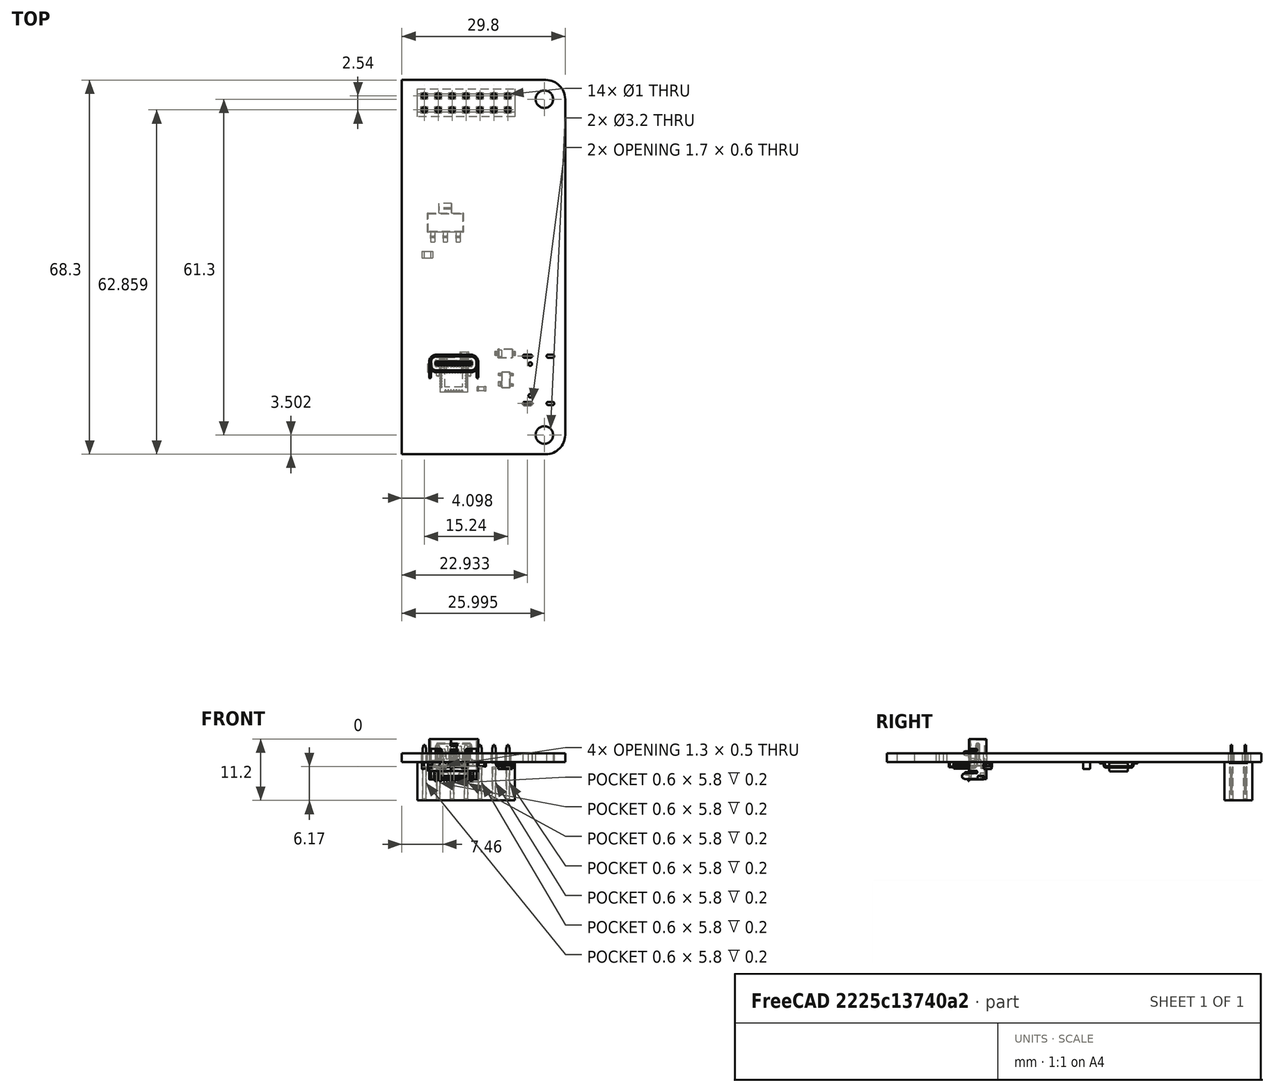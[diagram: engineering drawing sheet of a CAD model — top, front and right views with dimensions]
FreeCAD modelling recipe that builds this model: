
FCSTD DOCUMENT  (FreeCAD 1.0R39109 (Git))
Label: hautDeForme
License: All rights reserved
LicenseURL: http://en.wikipedia.org/wiki/All_rights_reserved
objects: Part::Feature×54, App::Link×18, App::Part×6, PartDesign::CoordinateSystem×1, Sketcher::SketchObject×1
note: 57 computed .brp shape members not serialized (recipe doc carries the construction recipe); baked Part::Feature solids carry a one-line shape summary decoded from their .brp

FEATURE [PartDesign::CoordinateSystem] Local_CS_adfa
  AttacherType = Attacher::AttachEngine3D
  MapMode = 2
FEATURE [Part::Feature] Pcb_adfa
  Placement = pos=(-130.277,147.371,0) rot=(0,0,1;0rad)
  shape: bbox 29.8 x 68.3 x 1.6 mm, 50 faces (baked)
FEATURE [Sketcher::SketchObject] PCB_Sketch_adfa
  ArcFitTolerance = 1e-06
  FullyConstrained = false
  MakeInternals = false
  sketch-geometry (6):
    g0: LineSegment StartX=-9.4646 StartY=-14.8382 StartZ=0 EndX=-9.4646 EndY=53.4618 EndZ=0
    g1: LineSegment StartX=16.8354 StartY=53.4618 StartZ=0 EndX=-9.4646 EndY=53.4618 EndZ=0
    g2: LineSegment StartX=20.3354 StartY=49.9618 StartZ=0 EndX=20.3354 EndY=-11.3382 EndZ=0
    g3: LineSegment StartX=16.8354 StartY=-14.8382 StartZ=0 EndX=-9.4646 EndY=-14.8382 EndZ=0
    g4: ArcOfCircle CenterX=16.8354 CenterY=49.9618 CenterZ=0 NormalX=0 NormalY=0 NormalZ=-1 AngleXU=1.5708 Radius=3.5 StartAngle=0 EndAngle=1.5708
    g5: ArcOfCircle CenterX=16.8354 CenterY=-11.3382 CenterZ=0 NormalX=0 NormalY=0 NormalZ=-1 AngleXU=3.14159 Radius=3.5 StartAngle=0 EndAngle=1.5708
  constraints (6):
    c: Coincident(g0,g3)
    c: Coincident(g0,g1)
    c: Coincident(g3,g5)
    c: Coincident(g1,g4)
    c: Coincident(g2,g5)
    c: Coincident(g2,g4)
FEATURE [App::Part] Board_Geoms_adfa
  Group = -> [Pcb_adfa,PCB_Sketch_adfa]
  Origin = -> Origin
FEATURE [Part::Feature] Shape  label="C14_C_0603_1608Metric_466b06563dad"
  Placement = pos=(5.08,-2.921,-1.6) rot=(0,1,0;3.14159rad)
  shape: bbox 1.6 x 0.8 x 0.8 mm, 28 faces (baked)
FEATURE [Part::Feature] Shape001  label="C6_C_0805_2012Metric_36fd2068b96d"
  Placement = pos=(-4.826,21.59,-1.6) rot=(1,0,0;3.14159rad)
  shape: bbox 2 x 1.25 x 1.25 mm, 28 faces (baked)
FEATURE [Part::Feature] Shape002  label="R26_R_0603_1608Metric_7708bdc434fe"
  Placement = pos=(1.905,3.429,-1.6) rot=(1,0,0;3.14159rad)
  shape: bbox 1.6 x 0.8 x 0.45 mm, 26 faces (baked)
FEATURE [App::Link] C6_C_0805_2012Metric_36fd2068b96d_ln_  label="C16_C_0805_2012Metric_426e6888749c"
  LinkPlacement = pos=(9.652,5.969,-1.6) rot=(1,0,0;3.14159rad)
  LinkedObject = -> Shape001
  Placement = pos=(9.652,5.969,-1.6) rot=(1,0,0;3.14159rad)
FEATURE [App::Link] C6_C_0805_2012Metric_36fd2068b96d_ln_001  label="C7_C_0805_2012Metric_e14df2acbac5"
  LinkPlacement = pos=(-0.635,21.59,-1.6) rot=(0,1,0;3.14159rad)
  LinkedObject = -> Shape001
  Placement = pos=(-0.635,21.59,-1.6) rot=(0,1,0;3.14159rad)
FEATURE [App::Link] R26_R_0603_1608Metric_7708bdc434fe_ln_  label="R24_R_0603_1608Metric_e1f34a9d9af8"
  LinkPlacement = pos=(0.508,-6.096,-1.6) rot=(0.707107,-0.707107,0;3.14159rad)
  LinkedObject = -> Shape002
  Placement = pos=(0.508,-6.096,-1.6) rot=(0.707107,-0.707107,0;3.14159rad)
FEATURE [Part::Feature] Shape003  label="D9_LED_0603_1608Metric_46d654ef8e3e"
  Placement = pos=(-4.318,0.889,-1.6) rot=(0.707107,0.707107,0;3.14159rad)
  shape: bbox 0.8 x 1.6 x 1.1 mm, 50 faces (baked)
FEATURE [Part::Feature] Shape004  label="J1_PinSocket_2x07_P254mm_Vertical_6ab3e544b67c"
  Placement = pos=(9.8784,50.5588,-1.6) rot=(0.707107,0.707107,0;3.14159rad)
  shape: bbox 17.78 x 5.08 x 10.1 mm, 444 faces (baked)
FEATURE [App::Link] C14_C_0603_1608Metric_466b06563dad_ln_  label="C15_C_0603_1608Metric_0d21c20a43dc"
  LinkPlacement = pos=(5.969,4.318,-1.6) rot=(0.707107,-0.707107,0;3.14159rad)
  LinkedObject = -> Shape
  Placement = pos=(5.969,4.318,-1.6) rot=(0.707107,-0.707107,0;3.14159rad)
FEATURE [Part::Feature] Shape005  label="U2_SOT_223_cc65569aa0fe"
  Placement = pos=(-1.524,27.432,-1.6) rot=(0.707107,0.707107,0;3.14159rad)
  shape: bbox 6.5 x 7 x 1.7 mm, 78 faces (baked)
FEATURE [App::Link] R26_R_0603_1608Metric_7708bdc434fe_ln_001  label="R27_R_0603_1608Metric_c96fc7131dde"
  LinkPlacement = pos=(-1.397,3.429,-1.6) rot=(0,1,0;3.14159rad)
  LinkedObject = -> Shape002
  Placement = pos=(-1.397,3.429,-1.6) rot=(0,1,0;3.14159rad)
FEATURE [App::Link] R26_R_0603_1608Metric_7708bdc434fe_ln_002  label="R35_R_0603_1608Metric_f47ad657d3cf"
  LinkPlacement = pos=(-6.096,-2.413,-1.6) rot=(0.707107,-0.707107,0;3.14159rad)
  LinkedObject = -> Shape002
  Placement = pos=(-6.096,-2.413,-1.6) rot=(0.707107,-0.707107,0;3.14159rad)
FEATURE [App::Link] R26_R_0603_1608Metric_7708bdc434fe_ln_003  label="R34_R_0603_1608Metric_230fafb0b39b"
  LinkPlacement = pos=(-6.096,0.889,-1.6) rot=(0.707107,0.707107,0;3.14159rad)
  LinkedObject = -> Shape002
  Placement = pos=(-6.096,0.889,-1.6) rot=(0.707107,0.707107,0;3.14159rad)
FEATURE [App::Link] R26_R_0603_1608Metric_7708bdc434fe_ln_004  label="R29_R_0603_1608Metric_0ce4d2b71c9b"
  LinkPlacement = pos=(12.573,-7.366,-1.6) rot=(0,1,0;3.14159rad)
  LinkedObject = -> Shape002
  Placement = pos=(12.573,-7.366,-1.6) rot=(0,1,0;3.14159rad)
FEATURE [App::Link] R26_R_0603_1608Metric_7708bdc434fe_ln_005  label="R25_R_0603_1608Metric_e44b7830c810"
  LinkPlacement = pos=(-1.27,-6.096,-1.6) rot=(0.707107,0.707107,0;3.14159rad)
  LinkedObject = -> Shape002
  Placement = pos=(-1.27,-6.096,-1.6) rot=(0.707107,0.707107,0;3.14159rad)
FEATURE [Part::Feature] Shape006  label="U4_QFN-28-1EP_5x5mm_Pitch0.5mm_e0a1b5ef8927"
  Placement = pos=(2e-16,-1.016,-1.6) rot=(0,1,0;3.14159rad)
  shape: bbox 5 x 5 x 0.92 mm, 182 faces (baked)
FEATURE [Part::Feature] Shape007  label="D14_D_SOD_123_b6459e2e886b"
  Placement = pos=(9.398,3.556,-1.6) rot=(1,0,0;3.14159rad)
  shape: bbox 3.8 x 1.6 x 1.25 mm, 67 faces (baked)
FEATURE [Part::Feature] Part__Feature  label="USB4105GFA_USB4105GFA"
  Placement = pos=(0,3e-16,-1.255) rot=(0,0,1;0rad)
  shape: bbox 0.25 x 0.05 x 2.38 mm, 6 faces (baked)
FEATURE [Part::Feature] Part__Feature001  label="USB4105GFA_USB4105GFA001"
  Placement = pos=(0,3e-16,-1.255) rot=(0,0,1;0rad)
  shape: bbox 0.25 x 0.05 x 2.38 mm, 6 faces (baked)
FEATURE [Part::Feature] Part__Feature002  label="USB4105GFA_USB4105GFA002"
  Placement = pos=(0,3e-16,-1.255) rot=(0,0,1;0rad)
  shape: bbox 0.25 x 0.05 x 1.88 mm, 6 faces (baked)
FEATURE [Part::Feature] Part__Feature003  label="USB4105GFA_USB4105GFA003"
  Placement = pos=(0,3e-16,-1.255) rot=(0,0,1;0rad)
  shape: bbox 0.25 x 0.05 x 1.88 mm, 6 faces (baked)
FEATURE [Part::Feature] Part__Feature004  label="USB4105GFA_USB4105GFA004"
  Placement = pos=(0,3e-16,-1.255) rot=(0,0,1;0rad)
  shape: bbox 0.25 x 0.05 x 1.88 mm, 6 faces (baked)
FEATURE [Part::Feature] Part__Feature005  label="USB4105GFA_USB4105GFA005"
  Placement = pos=(0,3e-16,-1.255) rot=(0,0,1;0rad)
  shape: bbox 0.25 x 0.05 x 1.88 mm, 6 faces (baked)
FEATURE [Part::Feature] Part__Feature006  label="USB4105GFA_USB4105GFA006"
  Placement = pos=(0,3e-16,-1.255) rot=(0,0,1;0rad)
  shape: bbox 0.25 x 0.05 x 1.88 mm, 6 faces (baked)
FEATURE [Part::Feature] Part__Feature007  label="USB4105GFA_USB4105GFA007"
  Placement = pos=(0,3e-16,-1.255) rot=(0,0,1;0rad)
  shape: bbox 0.25 x 0.05 x 1.88 mm, 6 faces (baked)
FEATURE [Part::Feature] Part__Feature008  label="USB4105GFA_USB4105GFA008"
  Placement = pos=(0,3e-16,-1.255) rot=(0,0,1;0rad)
  shape: bbox 0.25 x 0.05 x 1.88 mm, 6 faces (baked)
FEATURE [Part::Feature] Part__Feature009  label="USB4105GFA_USB4105GFA009"
  Placement = pos=(0,3e-16,-1.255) rot=(0,0,1;0rad)
  shape: bbox 0.25 x 0.05 x 1.88 mm, 6 faces (baked)
FEATURE [Part::Feature] Part__Feature010  label="USB4105GFA_USB4105GFA010"
  Placement = pos=(0,3e-16,-1.255) rot=(0,0,1;0rad)
  shape: bbox 0.25 x 0.05 x 2.38 mm, 6 faces (baked)
FEATURE [Part::Feature] Part__Feature011  label="USB4105GFA_USB4105GFA011"
  Placement = pos=(0,3e-16,-1.255) rot=(0,0,1;0rad)
  shape: bbox 0.25 x 0.05 x 2.38 mm, 6 faces (baked)
FEATURE [Part::Feature] Part__Feature012  label="USB4105GFA_USB4105GFA012"
  Placement = pos=(0,3e-16,-1.255) rot=(0,0,1;0rad)
  shape: bbox 0.25 x 0.05 x 2.38 mm, 6 faces (baked)
FEATURE [Part::Feature] Part__Feature013  label="USB4105GFA_USB4105GFA013"
  Placement = pos=(0,3e-16,-1.255) rot=(0,0,1;0rad)
  shape: bbox 0.25 x 0.05 x 1.88 mm, 6 faces (baked)
FEATURE [Part::Feature] Part__Feature014  label="USB4105GFA_USB4105GFA014"
  Placement = pos=(0,3e-16,-1.255) rot=(0,0,1;0rad)
  shape: bbox 0.25 x 0.05 x 1.88 mm, 6 faces (baked)
FEATURE [Part::Feature] Part__Feature015  label="USB4105GFA_USB4105GFA015"
  Placement = pos=(0,3e-16,-1.255) rot=(0,0,1;0rad)
  shape: bbox 0.25 x 0.05 x 2.38 mm, 6 faces (baked)
FEATURE [Part::Feature] Part__Feature016  label="USB4105GFA_USB4105GFA016"
  Placement = pos=(0,3e-16,-1.255) rot=(0,0,1;0rad)
  shape: bbox 0.25 x 0.05 x 1.88 mm, 6 faces (baked)
FEATURE [Part::Feature] Part__Feature017  label="USB4105GFA_USB4105GFA017"
  Placement = pos=(0,3e-16,-1.255) rot=(0,0,1;0rad)
  shape: bbox 0.25 x 0.05 x 1.88 mm, 6 faces (baked)
FEATURE [Part::Feature] Part__Feature018  label="USB4105GFA_USB4105GFA018"
  Placement = pos=(0,3e-16,-1.255) rot=(0,0,1;0rad)
  shape: bbox 0.25 x 0.05 x 1.88 mm, 6 faces (baked)
FEATURE [Part::Feature] Part__Feature019  label="USB4105GFA_USB4105GFA019"
  Placement = pos=(0,3e-16,-1.255) rot=(0,0,1;0rad)
  shape: bbox 0.25 x 0.05 x 1.88 mm, 6 faces (baked)
FEATURE [Part::Feature] Part__Feature020  label="USB4105GFA_USB4105GFA020"
  Placement = pos=(0,3e-16,-1.255) rot=(0,0,1;0rad)
  shape: bbox 0.25 x 0.05 x 2.38 mm, 6 faces (baked)
FEATURE [Part::Feature] Part__Feature021  label="USB4105GFA_USB4105GFA021"
  Placement = pos=(0,3e-16,-1.255) rot=(0,0,1;0rad)
  shape: bbox 0.25 x 0.05 x 1.88 mm, 6 faces (baked)
FEATURE [Part::Feature] Part__Feature022  label="USB4105GFA_USB4105GFA022"
  Placement = pos=(0,3e-16,-1.255) rot=(0,0,1;0rad)
  shape: bbox 0.25 x 0.05 x 1.88 mm, 6 faces (baked)
FEATURE [Part::Feature] Part__Feature023  label="USB4105GFA_USB4105GFA023"
  Placement = pos=(0,3e-16,-1.255) rot=(0,0,1;0rad)
  shape: bbox 0.25 x 0.05 x 2.38 mm, 6 faces (baked)
FEATURE [Part::Feature] Part__Feature024  label="USB4105GFA_USB4105GFA024"
  Placement = pos=(0,3e-16,-1.255) rot=(0,0,1;0rad)
  shape: bbox 0.35 x 0.1 x 1.82 mm, 9 faces (baked)
FEATURE [Part::Feature] Part__Feature025  label="USB4105GFA_USB4105GFA025"
  Placement = pos=(0,3e-16,-1.255) rot=(0,0,1;0rad)
  shape: bbox 0.35 x 0.1 x 1.82 mm, 9 faces (baked)
FEATURE [Part::Feature] Part__Feature026  label="USB4105GFA_USB4105GFA026"
  Placement = pos=(0,3e-16,-1.255) rot=(0,0,1;0rad)
  shape: bbox 0.2 x 0.32 x 0.725 mm, 10 faces (baked)
FEATURE [Part::Feature] Part__Feature027  label="USB4105GFA_USB4105GFA027"
  Placement = pos=(0,3e-16,-1.255) rot=(0,0,1;0rad)
  shape: bbox 0.2 x 0.32 x 0.725 mm, 10 faces (baked)
FEATURE [Part::Feature] Part__Feature028  label="USB4105GFA_USB4105GFA028"
  Placement = pos=(0,3e-16,-1.255) rot=(0,0,1;0rad)
  shape: bbox 0.2 x 0.32 x 0.725 mm, 10 faces (baked)
FEATURE [Part::Feature] Part__Feature029  label="USB4105GFA_USB4105GFA029"
  Placement = pos=(0,3e-16,-1.255) rot=(0,0,1;0rad)
  shape: bbox 0.2 x 0.32 x 0.725 mm, 10 faces (baked)
FEATURE [Part::Feature] Part__Feature030  label="USB4105GFA_USB4105GFA030"
  Placement = pos=(0,3e-16,-1.255) rot=(0,0,1;0rad)
  shape: bbox 0.2 x 0.32 x 0.725 mm, 10 faces (baked)
FEATURE [Part::Feature] Part__Feature031  label="USB4105GFA_USB4105GFA031"
  Placement = pos=(0,3e-16,-1.255) rot=(0,0,1;0rad)
  shape: bbox 0.2 x 0.32 x 0.725 mm, 10 faces (baked)
FEATURE [Part::Feature] Part__Feature032  label="USB4105GFA_USB4105GFA032"
  Placement = pos=(0,3e-16,-1.255) rot=(0,0,1;0rad)
  shape: bbox 0.2 x 0.32 x 0.725 mm, 10 faces (baked)
FEATURE [Part::Feature] Part__Feature033  label="USB4105GFA_USB4105GFA033"
  Placement = pos=(0,3e-16,-1.255) rot=(0,0,1;0rad)
  shape: bbox 0.2 x 0.32 x 0.725 mm, 10 faces (baked)
FEATURE [Part::Feature] Part__Feature034  label="USB4105GFA_USB4105GFA034"
  Placement = pos=(0,3e-16,-1.255) rot=(0,0,1;0rad)
  shape: bbox 0.2 x 0.32 x 0.725 mm, 10 faces (baked)
FEATURE [Part::Feature] Part__Feature035  label="USB4105GFA_USB4105GFA035"
  Placement = pos=(0,3e-16,-1.255) rot=(0,0,1;0rad)
  shape: bbox 0.2 x 0.32 x 0.725 mm, 10 faces (baked)
FEATURE [Part::Feature] Part__Feature036  label="USB4105GFA_USB4105GFA036"
  Placement = pos=(0,3e-16,-1.255) rot=(0,0,1;0rad)
  shape: bbox 0.2 x 0.32 x 0.725 mm, 10 faces (baked)
FEATURE [Part::Feature] Part__Feature037  label="USB4105GFA_USB4105GFA037"
  Placement = pos=(0,3e-16,-1.255) rot=(0,0,1;0rad)
  shape: bbox 0.2 x 0.32 x 0.725 mm, 10 faces (baked)
FEATURE [Part::Feature] Part__Feature038  label="USB4105GFA_USB4105GFA038"
  Placement = pos=(0,3e-16,-1.255) rot=(0,0,1;0rad)
  shape: bbox 0.2 x 0.32 x 0.725 mm, 10 faces (baked)
FEATURE [Part::Feature] Part__Feature039  label="USB4105GFA_USB4105GFA039"
  Placement = pos=(0,3e-16,-1.255) rot=(0,0,1;0rad)
  shape: bbox 0.2 x 0.32 x 0.725 mm, 10 faces (baked)
FEATURE [Part::Feature] Part__Feature040  label="USB4105GFA_USB4105GFA040"
  Placement = pos=(0,3e-16,-1.255) rot=(0,0,1;0rad)
  shape: bbox 0.2 x 0.32 x 0.725 mm, 10 faces (baked)
FEATURE [Part::Feature] Part__Feature041  label="USB4105GFA_USB4105GFA041"
  Placement = pos=(0,3e-16,-1.255) rot=(0,0,1;0rad)
  shape: bbox 0.2 x 0.32 x 0.725 mm, 10 faces (baked)
FEATURE [Part::Feature] Part__Feature042  label="USB4105GFA_USB4105GFA042"
  Placement = pos=(0,3e-16,-1.255) rot=(0,0,1;0rad)
  shape: bbox 8.94 x 4.41 x 7.33 mm, 421 faces (baked)
FEATURE [Part::Feature] Part__Feature043  label="USB4105GFA_USB4105GFA043"
  Placement = pos=(0,3e-16,-1.255) rot=(0,0,1;0rad)
  shape: bbox 8.89 x 3.61 x 6.57 mm, 162 faces (baked)
FEATURE [App::Part] USB4105GFA_USB4105GFA  label="USB4105GFA_USB4105GFA044"
  Group = -> [Part__Feature,Part__Feature001,Part__Feature002,Part__Feature003,Part__Feature004,Part__Feature005,Part__Feature006,Part__Feature007,Part__Feature008,Part__Feature009,Part__Feature010,Part__Feature011,Part__Feature012,Part__Feature013,Part__Feature014,Part__Feature015,Part__Feature016,Part__Feature017,Part__Feature018,Part__Feature019,Part__Feature020,Part__Feature021,Part__Feature022,+21 more]
  Origin = -> Origin008
FEATURE [App::Part] USB4105GFA  label="J6_USB4105GFA_c17b99680fba"
  Group = -> [USB4105GFA_USB4105GFA]
  Origin = -> Origin009
  Placement = pos=(17.653,-1.27,-1.6) rot=(0.57735,-0.57735,0.57735;4.18879rad)
FEATURE [Part::Feature] Shape008  label="D8_SOT_143_8c8184d03dee"
  Placement = pos=(9.525,-1.27,-1.6) rot=(1,0,0;3.14159rad)
  shape: bbox 2.8 x 2.9 x 1.2 mm, 94 faces (baked)
FEATURE [App::Link] D9_LED_0603_1608Metric_46d654ef8e3e_ln_  label="D6_LED_0603_1608Metric_febbf15eef76"
  LinkPlacement = pos=(8.509,35.941,-1.6) rot=(0.707107,-0.707107,0;3.14159rad)
  LinkedObject = -> Shape003
  Placement = pos=(8.509,35.941,-1.6) rot=(0.707107,-0.707107,0;3.14159rad)
FEATURE [App::Link] R26_R_0603_1608Metric_7708bdc434fe_ln_006  label="R30_R_0603_1608Metric_fa79a0fc6f2e"
  LinkPlacement = pos=(9.652,-3.937,-1.6) rot=(0,1,0;3.14159rad)
  LinkedObject = -> Shape002
  Placement = pos=(9.652,-3.937,-1.6) rot=(0,1,0;3.14159rad)
FEATURE [App::Link] R26_R_0603_1608Metric_7708bdc434fe_ln_007  label="R6_R_0603_1608Metric_d2128f492321"
  LinkPlacement = pos=(10.414,35.941,-1.6) rot=(0.707107,-0.707107,0;3.14159rad)
  LinkedObject = -> Shape002
  Placement = pos=(10.414,35.941,-1.6) rot=(0.707107,-0.707107,0;3.14159rad)
FEATURE [App::Link] R26_R_0603_1608Metric_7708bdc434fe_ln_008  label="R28_R_0603_1608Metric_f90188b88249"
  LinkPlacement = pos=(9.271,1.397,-1.6) rot=(1,0,0;3.14159rad)
  LinkedObject = -> Shape002
  Placement = pos=(9.271,1.397,-1.6) rot=(1,0,0;3.14159rad)
FEATURE [App::Link] C14_C_0603_1608Metric_466b06563dad_ln_001  label="C13_C_0603_1608Metric_5dbe2ea53268"
  LinkPlacement = pos=(5.08,-4.699,-1.6) rot=(0,1,0;3.14159rad)
  LinkedObject = -> Shape
  Placement = pos=(5.08,-4.699,-1.6) rot=(0,1,0;3.14159rad)
FEATURE [App::Link] R26_R_0603_1608Metric_7708bdc434fe_ln_009  label="R23_R_0603_1608Metric_dabb29a5a1b6"
  LinkPlacement = pos=(2.286,-6.096,-1.6) rot=(0.707107,0.707107,0;3.14159rad)
  LinkedObject = -> Shape002
  Placement = pos=(2.286,-6.096,-1.6) rot=(0.707107,0.707107,0;3.14159rad)
FEATURE [App::Link] R26_R_0603_1608Metric_7708bdc434fe_ln_010  label="R5_R_0603_1608Metric_7c59e7465914"
  LinkPlacement = pos=(-6.35,27.94,-1.6) rot=(0.707107,-0.707107,0;3.14159rad)
  LinkedObject = -> Shape002
  Placement = pos=(-6.35,27.94,-1.6) rot=(0.707107,-0.707107,0;3.14159rad)
FEATURE [App::Link] D9_LED_0603_1608Metric_46d654ef8e3e_ln_001  label="D11_LED_0603_1608Metric_9cf470dc25c5"
  LinkPlacement = pos=(-4.318,-2.413,-1.6) rot=(0.707107,-0.707107,0;3.14159rad)
  LinkedObject = -> Shape003
  Placement = pos=(-4.318,-2.413,-1.6) rot=(0.707107,-0.707107,0;3.14159rad)
FEATURE [App::Link] D9_LED_0603_1608Metric_46d654ef8e3e_ln_002  label="D5_LED_0603_1608Metric_95d6e158d9c7"
  LinkPlacement = pos=(-6.35,24.511,-1.6) rot=(0.707107,0.707107,0;3.14159rad)
  LinkedObject = -> Shape003
  Placement = pos=(-6.35,24.511,-1.6) rot=(0.707107,0.707107,0;3.14159rad)
FEATURE [App::Part] Bot_adfa
  Group = -> [Shape,Shape001,Shape002,C6_C_0805_2012Metric_36fd2068b96d_ln_,C6_C_0805_2012Metric_36fd2068b96d_ln_001,R26_R_0603_1608Metric_7708bdc434fe_ln_,Shape003,Shape004,C14_C_0603_1608Metric_466b06563dad_ln_,Shape005,R26_R_0603_1608Metric_7708bdc434fe_ln_001,R26_R_0603_1608Metric_7708bdc434fe_ln_002,R26_R_0603_1608Metric_7708bdc434fe_ln_003,R26_R_0603_1608Metric_7708bdc434fe_ln_004,+14 more]
  Origin = -> Origin004
FEATURE [App::Part] Step_Models_adfa
  Group = -> [Bot_adfa]
  Origin = -> Origin002
FEATURE [App::Part] Board_adfa  label="hautDeForme"
  Group = -> [Local_CS_adfa,Board_Geoms_adfa,Step_Models_adfa]
  Origin = -> Origin001
